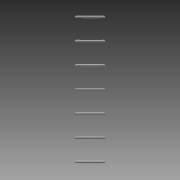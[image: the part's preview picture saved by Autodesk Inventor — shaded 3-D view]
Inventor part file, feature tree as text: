
AUTODESK INVENTOR PART (.ipt)
format: ipt  version: 2015 (Build 190159000, 159)  size: 94,720 bytes
history: native  units: in
note: dims shown in document units (in); Inventor stores cm internally (conversion verified against a paired STEP export)
features: sketch x2, other x1, loft x1, pattern_linear x1
ambient origin geometry x8: Origin, YZ Plane, XZ Plane, XY Plane, X Axis, Y Axis, Z Axis, Center Point
bodies: Solid1 (feature_tree)
feature tree (5):
  other  "Work Axis1"
  loft  "Loft1"
  pattern_linear  "Rectangular Pattern1"  Spacing1=2.75in  [1 undecoded]
  sketch  "Sketch1"  dims[d2=0.375in d3=2.75in]
  sketch  "Sketch2"  dims[d4=0.375in d5=2.75in d6=0.0in d7=90.0deg d8=0.0in d9=90.0deg d22=2.7559in d24=4.0in]
note: 1 required parameter value undecoded (feature->parameter linkage not recoverable at this tier; creation-order binding heuristic only, values carry confidence <= 0.55)
